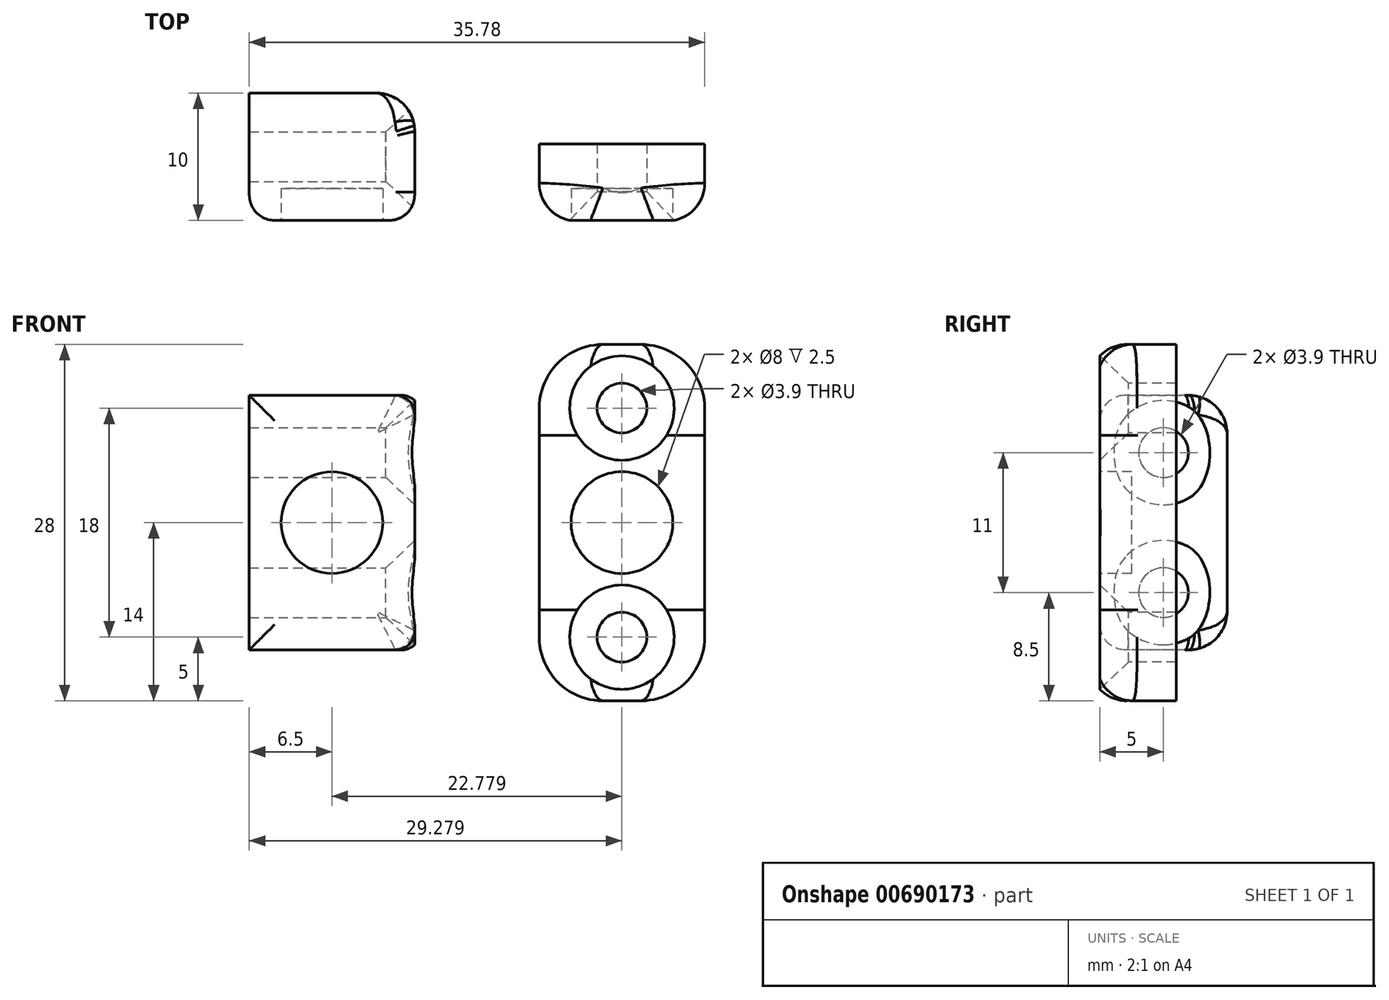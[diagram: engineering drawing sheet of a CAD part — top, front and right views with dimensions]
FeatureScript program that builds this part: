
annotation { "Feature Type Name" : "Feature", "Feature Type Description" : "" }
export const myFeature = defineFeature(function(context is Context, id is Id, definition is map)
    precondition{}
    {
        {
            var Q0;
            Q0=qCreatedBy(makeId("Front.planeOp"),FACE);
            var sketch = newSketch(context, id + "F0", { "sketchPlane" : qUnion([Q0])});
            skCircle(sketch, "E0", {"center": v(0, 0) * mm, "radius": 4 * mm});
            skLineSegment(sketch, "E1.bottom", {"start": v(-6.5, -10) * mm, "end": v(6.5, -10) * mm});
            skLineSegment(sketch, "E1.top", {"start": v(-6.5, 10) * mm, "end": v(6.5, 10) * mm});
            skLineSegment(sketch, "E1.left", {"start": v(-6.5, -10) * mm, "end": v(-6.5, 10) * mm});
            skLineSegment(sketch, "E1.right", {"start": v(6.5, -10) * mm, "end": v(6.5, 10) * mm});
            skLineSegment(sketch, "E2.bottom", {"start": v(29.28, 14) * mm, "end": v(16.28, 14) * mm});
            skLineSegment(sketch, "E2.top", {"start": v(29.28, -14) * mm, "end": v(16.28, -14) * mm});
            skLineSegment(sketch, "E2.left", {"start": v(29.28, 14) * mm, "end": v(29.28, -14) * mm});
            skLineSegment(sketch, "E2.right", {"start": v(16.28, 14) * mm, "end": v(16.28, -14) * mm});
            skPoint(sketch, "E2.middle", {"position": v(22.78, 0) * mm});
            skCircle(sketch, "E3", {"center": v(22.78, 0) * mm, "radius": 4 * mm});
            skLineSegment(sketch, "E4", {"start": v(22.78, -14) * mm, "end": v(22.78, 14) * mm, "construction": true});
            skPoint(sketch, "E5", {"position": v(22.78, -9) * mm});
            skPoint(sketch, "E6", {"position": v(22.78, 9) * mm});
            skSolve(sketch);
        }
        {
            var Q0;
            Q0=makeQuery(id+"F0.imprint","IMPRINT",FACE,{"disambiguationData":[TD([[makeQuery(id+"F0.imprint","IMPRINT",EDGE,{"derivedFrom":sQuery(id+"F0.wireOp",EDGE,"E0")}),-1.0]])]});
            var Q1;
            Q1=makeQuery(id+"F0.imprint","IMPRINT",FACE,{"disambiguationData":[TD([[makeQuery(id+"F0.imprint","IMPRINT",EDGE,{"derivedFrom":sQuery(id+"F0.wireOp",EDGE,"E0")}),1.0]])]});
            extrude(context, id + "F1", {"entities" : qUnion([Q0, Q1]), "oppositeDirection" : true, "depth" : 10 * mm, "offsetDistance" : 25 * mm});
        }
        {
            var Q0;
            Q0=makeQuery(id+"F0.imprint","IMPRINT",FACE,{"disambiguationData":[TD([[makeQuery(id+"F0.imprint","IMPRINT",EDGE,{"derivedFrom":sQuery(id+"F0.wireOp",EDGE,"E0")}),1.0]])]});
            extrude(context, id + "F2", {"entities" : qUnion([Q0]), "operationType" : NewBodyOperationType.REMOVE, "oppositeDirection" : true, "depth" : 2.5 * mm, "offsetDistance" : 25 * mm});
        }
        {
            var Q0;
            Q0=makeQuery(id+"F1.opExtrude","SWEPT_FACE",FACE,{"disambiguationData":[OSD([sQuery(id+"F0.wireOp",EDGE,"E1.right")])]});
            var sketch = newSketch(context, id + "F3", { "sketchPlane" : qUnion([Q0])});
            skLineSegment(sketch, "E7", {"start": v(5, 10) * mm, "end": v(5, -10) * mm, "construction": true});
            skPoint(sketch, "E8", {"position": v(5, 5.5) * mm});
            skPoint(sketch, "E9", {"position": v(5, -5.5) * mm});
            skSolve(sketch);
        }
        {
            var Q0;
            Q0=sQuery(id+"F3.wireOp",VERTEX,"E8");
            var Q1;
            Q1=makeQuery(id+"F1.opExtrude","SWEPT_BODY",BODY,{"disambiguationData":[OSD([sQuery(id+"F0.wireOp",EDGE,"E1.bottom"),sQuery(id+"F0.wireOp",EDGE,"E1.top"),sQuery(id+"F0.wireOp",EDGE,"E1.left"),sQuery(id+"F0.wireOp",EDGE,"E1.right")])]});
            hole(context, id + "F4", {"style" : HoleStyle.C_SINK, "endStyle" : HoleEndStyle.THROUGH, "holeDiameter" : 3.9 * mm, "cSinkDiameter" : 8.2 * mm, "cSinkAngle" : 87 * degree, "majorDiameter" : 5 * mm, "isTappedThrough" : true, "tappedDepth" : 12 * mm, "tapClearance" : 3, "startFromSketch" : true, "locations" : qUnion([Q0]), "scope" : qUnion([Q1])});
        }
        {
            var Q0;
            Q0=sQuery(id+"F3.wireOp",VERTEX,"E9");
            var Q1;
            Q1=makeQuery(id+"F1.opExtrude","SWEPT_BODY",BODY,{"disambiguationData":[OSD([sQuery(id+"F0.wireOp",EDGE,"E1.bottom"),sQuery(id+"F0.wireOp",EDGE,"E1.top"),sQuery(id+"F0.wireOp",EDGE,"E1.left"),sQuery(id+"F0.wireOp",EDGE,"E1.right")])]});
            hole(context, id + "F5", {"style" : HoleStyle.C_SINK, "endStyle" : HoleEndStyle.THROUGH, "holeDiameter" : 3.9 * mm, "cSinkDiameter" : 8.2 * mm, "cSinkAngle" : 87 * degree, "majorDiameter" : 5 * mm, "isTappedThrough" : true, "tappedDepth" : 12 * mm, "tapClearance" : 3, "startFromSketch" : true, "locations" : qUnion([Q0]), "scope" : qUnion([Q1])});
        }
        {
            var Q0;
            Q0=makeQuery(id+"F1.opExtrude","CAP_EDGE",EDGE,{"disambiguationData":[OSD([sQuery(id+"F0.wireOp",EDGE,"E1.top")])],"isStart":false});
            var Q1;
            Q1=makeQuery(id+"F1.opExtrude","CAP_EDGE",EDGE,{"disambiguationData":[OSD([sQuery(id+"F0.wireOp",EDGE,"E1.bottom")])],"isStart":false});
            var Q2;
            Q2=makeQuery(id+"F1.opExtrude","CAP_EDGE",EDGE,{"disambiguationData":[OSD([sQuery(id+"F0.wireOp",EDGE,"E1.right")])],"isStart":false});
            fillet(context, id + "F6", {"entities" : qUnion([Q0, Q1, Q2]), "radius" : 3 * mm, "tangentPropagation" : true, "allowEdgeOverflow" : false});
        }
        {
            var Q0;
            Q0=makeQuery(id+"F1.opExtrude","SWEPT_EDGE",EDGE,{"disambiguationData":[OSD([sQuery(id+"F0.wireOp",EDGE,"E1.bottom"),sQuery(id+"F0.wireOp",EDGE,"E1.right")])]});
            var Q1;
            Q1=makeQuery(id+"F1.opExtrude","SWEPT_EDGE",EDGE,{"disambiguationData":[OSD([sQuery(id+"F0.wireOp",EDGE,"E1.top"),sQuery(id+"F0.wireOp",EDGE,"E1.right")])]});
            fillet(context, id + "F7", {"entities" : qUnion([Q0, Q1]), "radius" : 1.5 * mm, "tangentPropagation" : true, "allowEdgeOverflow" : false});
        }
        {
            var Q0;
            Q0=makeQuery(id+"F0.imprint","IMPRINT",FACE,{"disambiguationData":[TD([[makeQuery(id+"F0.imprint","IMPRINT",EDGE,{"derivedFrom":sQuery(id+"F0.wireOp",EDGE,"E2.bottom")}),1.0]])]});
            var Q1;
            Q1=makeQuery(id+"F0.imprint","IMPRINT",FACE,{"disambiguationData":[TD([[makeQuery(id+"F0.imprint","IMPRINT",EDGE,{"derivedFrom":sQuery(id+"F0.wireOp",EDGE,"E3")}),1.0]])]});
            extrude(context, id + "F8", {"entities" : qUnion([Q0, Q1]), "oppositeDirection" : true, "depth" : 6 * mm, "offsetDistance" : 25 * mm});
        }
        {
            var Q0;
            Q0=makeQuery(id+"F0.imprint","IMPRINT",FACE,{"disambiguationData":[TD([[makeQuery(id+"F0.imprint","IMPRINT",EDGE,{"derivedFrom":sQuery(id+"F0.wireOp",EDGE,"E3")}),1.0]])]});
            extrude(context, id + "F9", {"entities" : qUnion([Q0]), "operationType" : NewBodyOperationType.REMOVE, "oppositeDirection" : true, "depth" : 2.5 * mm, "offsetDistance" : 25 * mm});
        }
        {
            var Q0;
            Q0=sQuery(id+"F0.wireOp",VERTEX,"E5");
            var Q1;
            Q1=sQuery(id+"F0.wireOp",VERTEX,"E6");
            var Q2;
            Q2=makeQuery(id+"F8.opExtrude","SWEPT_BODY",BODY,{"disambiguationData":[OSD([sQuery(id+"F0.wireOp",EDGE,"E2.bottom"),sQuery(id+"F0.wireOp",EDGE,"E2.top"),sQuery(id+"F0.wireOp",EDGE,"E2.left"),sQuery(id+"F0.wireOp",EDGE,"E2.right")])]});
            hole(context, id + "F10", {"style" : HoleStyle.C_SINK, "endStyle" : HoleEndStyle.THROUGH, "holeDiameter" : 3.9 * mm, "cSinkDiameter" : 8.2 * mm, "cSinkAngle" : 87 * degree, "majorDiameter" : 5 * mm, "isTappedThrough" : true, "tappedDepth" : 12 * mm, "tapClearance" : 3, "startFromSketch" : true, "locations" : qUnion([Q0, Q1]), "scope" : qUnion([Q2])});
        }
        {
            var Q0;
            Q0=makeQuery(id+"F8.opExtrude","SWEPT_EDGE",EDGE,{"disambiguationData":[OSD([sQuery(id+"F0.wireOp",EDGE,"E2.top"),sQuery(id+"F0.wireOp",EDGE,"E2.right")])]});
            var Q1;
            Q1=makeQuery(id+"F8.opExtrude","SWEPT_EDGE",EDGE,{"disambiguationData":[OSD([sQuery(id+"F0.wireOp",EDGE,"E2.top"),sQuery(id+"F0.wireOp",EDGE,"E2.left")])]});
            var Q2;
            Q2=makeQuery(id+"F8.opExtrude","SWEPT_EDGE",EDGE,{"disambiguationData":[OSD([sQuery(id+"F0.wireOp",EDGE,"E2.bottom"),sQuery(id+"F0.wireOp",EDGE,"E2.right")])]});
            var Q3;
            Q3=makeQuery(id+"F8.opExtrude","SWEPT_EDGE",EDGE,{"disambiguationData":[OSD([sQuery(id+"F0.wireOp",EDGE,"E2.bottom"),sQuery(id+"F0.wireOp",EDGE,"E2.left")])]});
            fillet(context, id + "F11", {"entities" : qUnion([Q0, Q1, Q2, Q3]), "radius" : 5 * mm, "tangentPropagation" : true, "allowEdgeOverflow" : false});
        }
        {
            var Q0;
            Q0=makeQuery(id+"F8.opExtrude","CAP_EDGE",EDGE,{"disambiguationData":[OSD([sQuery(id+"F0.wireOp",EDGE,"E2.left")])],"isStart":true});
            fillet(context, id + "F12", {"entities" : qUnion([Q0]), "radius" : 3 * mm, "tangentPropagation" : true, "allowEdgeOverflow" : false});
        }
        {
            var Q0;
            Q0=makeQuery(id+"F1.opExtrude","CAP_EDGE",EDGE,{"disambiguationData":[OSD([sQuery(id+"F0.wireOp",EDGE,"E1.bottom")])],"isStart":true});
            var Q1;
            Q1=makeQuery(id+"F1.opExtrude","CAP_EDGE",EDGE,{"disambiguationData":[OSD([sQuery(id+"F0.wireOp",EDGE,"E1.left")])],"isStart":true});
            fillet(context, id + "F13", {"entities" : qUnion([Q0, Q1]), "radius" : 2 * mm, "tangentPropagation" : true, "allowEdgeOverflow" : false});
        }
    });
